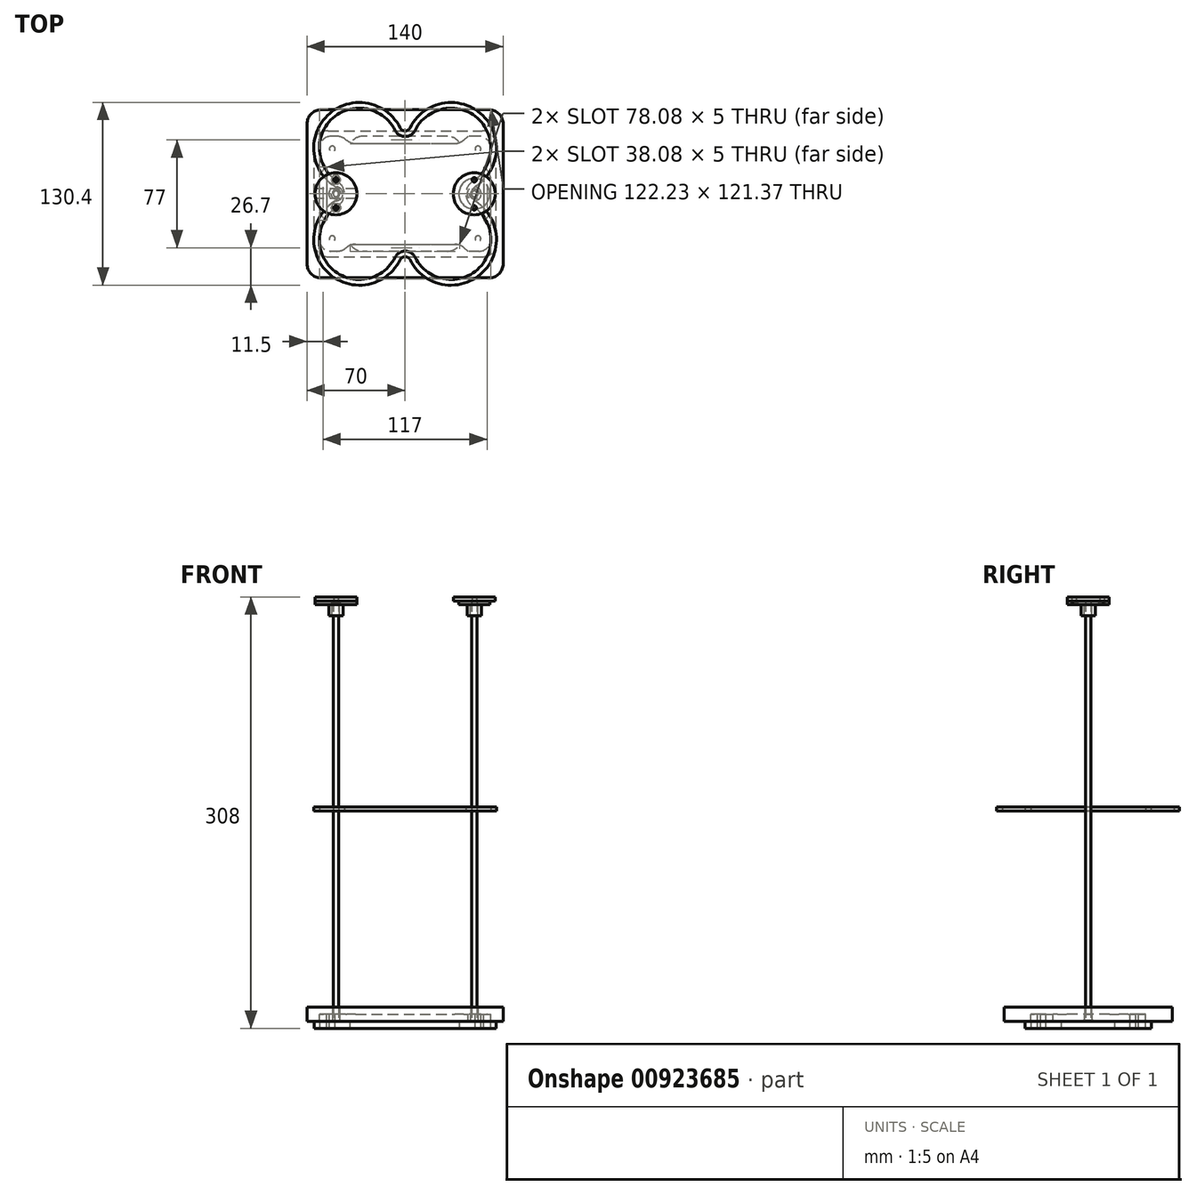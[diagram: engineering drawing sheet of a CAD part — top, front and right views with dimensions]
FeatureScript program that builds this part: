
annotation { "Feature Type Name" : "Feature", "Feature Type Description" : "" }
export const myFeature = defineFeature(function(context is Context, id is Id, definition is map)
    precondition{}
    {
        {
            var Q0;
            Q0=qCreatedBy(makeId("Top.planeOp"),FACE);
            var sketch = newSketch(context, id + "F0", { "sketchPlane" : qUnion([Q0])});
            skArc(sketch, "E0", {"start": v(50.3, 5.38) * mm, "mid": v(54.36, 56.94) * mm, "end": v(3.58, 47.14) * mm});
            skArc(sketch, "E1.MirrorC", {"start": v(-50.3, 5.38) * mm, "mid": v(-54.36, 56.94) * mm, "end": v(-3.58, 47.14) * mm});
            skArc(sketch, "E2.MirrorC", {"start": v(50.3, -5.38) * mm, "mid": v(54.36, -56.94) * mm, "end": v(3.58, -47.14) * mm});
            skArc(sketch, "E3.MirrorC", {"start": v(-50.3, -5.38) * mm, "mid": v(-54.36, -56.94) * mm, "end": v(-3.58, -47.14) * mm});
            skLineSegment(sketch, "E4", {"start": v(-32.7, -32.7) * mm, "end": v(32.7, 32.7) * mm, "construction": true});
            skArc(sketch, "E5", {"start": v(50.3, 5.38) * mm, "mid": v(47.37, 0) * mm, "end": v(50.3, -5.38) * mm});
            skArc(sketch, "E6.MirrorC", {"start": v(-50.3, 5.38) * mm, "mid": v(-47.37, 0) * mm, "end": v(-50.3, -5.38) * mm});
            skArc(sketch, "E7", {"start": v(-3.58, 47.14) * mm, "mid": v(0, 44.91) * mm, "end": v(3.58, 47.14) * mm});
            skArc(sketch, "E8.MirrorC", {"start": v(-3.58, -47.14) * mm, "mid": v(0, -44.91) * mm, "end": v(3.58, -47.14) * mm});
            skArc(sketch, "E9.0", {"start": v(-48.14, 8.74) * mm, "mid": v(-43.37, 0) * mm, "end": v(-48.14, -8.74) * mm});
            skArc(sketch, "E9.1", {"start": v(-48.14, -8.74) * mm, "mid": v(-51.7, -53.95) * mm, "end": v(-7.17, -45.36) * mm});
            skArc(sketch, "E9.2", {"start": v(-48.14, 8.74) * mm, "mid": v(-51.7, 53.95) * mm, "end": v(-7.17, 45.36) * mm});
            skArc(sketch, "E9.3", {"start": v(-7.17, -45.36) * mm, "mid": v(0, -40.91) * mm, "end": v(7.17, -45.36) * mm});
            skArc(sketch, "E9.4", {"start": v(-7.17, 45.36) * mm, "mid": v(0, 40.91) * mm, "end": v(7.17, 45.36) * mm});
            skArc(sketch, "E9.5", {"start": v(48.14, 8.74) * mm, "mid": v(51.7, 53.95) * mm, "end": v(7.17, 45.36) * mm});
            skArc(sketch, "E9.6", {"start": v(48.14, 8.74) * mm, "mid": v(43.37, 0) * mm, "end": v(48.14, -8.74) * mm});
            skArc(sketch, "E9.7", {"start": v(48.14, -8.74) * mm, "mid": v(51.7, -53.95) * mm, "end": v(7.17, -45.36) * mm});
            skSolve(sketch);
        }
        {
            var Q0;
            Q0 = qSketchRegion(id + "F0", true);
            extrude(context, id + "F1", {"entities" : qUnion([Q0]), "depth" : 3 * mm, "offsetDistance" : 25 * mm});
        }
        {
            var Q0;
            Q0=qCreatedBy(makeId("Top.planeOp"),FACE);
            var sketch = newSketch(context, id + "F2", { "sketchPlane" : qUnion([Q0])});
            skCircle(sketch, "E10", {"center": v(49.37, 0) * mm, "radius": 2 * mm});
            skCircle(sketch, "E11.MirrorC", {"center": v(-49.37, 0) * mm, "radius": 2 * mm});
            skSolve(sketch);
        }
        {
            var Q0;
            Q0 = qSketchRegion(id + "F2", true);
            extrude(context, id + "F3", {"entities" : qUnion([Q0]), "operationType" : NewBodyOperationType.ADD, "depth" : 150 * mm, "offsetDistance" : 25 * mm, "hasSecondDirection" : true, "secondDirectionOppositeDirection" : true, "secondDirectionDepth" : 150 * mm});
        }
        {
            var Q0;
            Q0=qCreatedBy(makeId("Top.planeOp"),FACE);
            cPlane(context, id + "F4", {"entities" : qUnion([Q0]), "cplaneType" : CPlaneType.OFFSET, "offset" : 150 * mm, "oppositeDirection" : true, "width" : 150 * mm, "height" : 150 * mm});
        }
        {
            var Q0;
            Q0=qCreatedBy(id+"F4.planeOp",FACE);
            var sketch = newSketch(context, id + "F5", { "sketchPlane" : qUnion([Q0])});
            skLineSegment(sketch, "E12.bottom", {"start": v(-65, -45) * mm, "end": v(65, -45) * mm});
            skLineSegment(sketch, "E12.top", {"start": v(-65, 45) * mm, "end": v(65, 45) * mm});
            skLineSegment(sketch, "E12.left", {"start": v(-65, -45) * mm, "end": v(-65, 45) * mm});
            skLineSegment(sketch, "E12.right", {"start": v(65, -45) * mm, "end": v(65, 45) * mm});
            skSolve(sketch);
        }
        {
            var Q0;
            Q0 = qSketchRegion(id + "F5", true);
            extrude(context, id + "F6", {"entities" : qUnion([Q0]), "oppositeDirection" : true, "depth" : 5 * mm, "offsetDistance" : 25 * mm});
        }
        {
            var Q0;
            Q0=makeQuery(id+"F6.opExtrude","SWEPT_EDGE",EDGE,{"disambiguationData":[OSD([sQuery(id+"F5.wireOp",EDGE,"E12.bottom"),sQuery(id+"F5.wireOp",EDGE,"E12.left")])]});
            var Q1;
            Q1=makeQuery(id+"F6.opExtrude","SWEPT_EDGE",EDGE,{"disambiguationData":[OSD([sQuery(id+"F5.wireOp",EDGE,"E12.top"),sQuery(id+"F5.wireOp",EDGE,"E12.left")])]});
            var Q2;
            Q2=makeQuery(id+"F6.opExtrude","SWEPT_EDGE",EDGE,{"disambiguationData":[OSD([sQuery(id+"F5.wireOp",EDGE,"E12.bottom"),sQuery(id+"F5.wireOp",EDGE,"E12.right")])]});
            var Q3;
            Q3=makeQuery(id+"F6.opExtrude","SWEPT_EDGE",EDGE,{"disambiguationData":[OSD([sQuery(id+"F5.wireOp",EDGE,"E12.top"),sQuery(id+"F5.wireOp",EDGE,"E12.right")])]});
            fillet(context, id + "F7", {"entities" : qUnion([Q0, Q1, Q2, Q3]), "radius" : 10 * mm, "tangentPropagation" : true, "allowEdgeOverflow" : false});
        }
        {
            var Q0;
            Q0=makeQuery(id+"F3.opExtrude","CAP_FACE",FACE,{"disambiguationData":[OSD([sQuery(id+"F2.wireOp",EDGE,"E10")])],"isStart":true});
            var sketch = newSketch(context, id + "F8", { "sketchPlane" : qUnion([Q0])});
            skCircle(sketch, "E13", {"center": v(49.37, 0) * mm, "radius": 3.5 * mm});
            skCircle(sketch, "E14.MirrorC", {"center": v(-49.37, 0) * mm, "radius": 3.5 * mm});
            skSolve(sketch);
        }
        {
            var Q0;
            Q0 = qSketchRegion(id + "F8", true);
            extrude(context, id + "F9", {"entities" : qUnion([Q0]), "operationType" : NewBodyOperationType.ADD, "oppositeDirection" : true, "depth" : 0.5 * mm, "offsetDistance" : 25 * mm});
        }
        {
            var Q0;
            Q0=qCreatedBy(id+"F4.planeOp",FACE);
            var sketch = newSketch(context, id + "F10", { "sketchPlane" : qUnion([Q0])});
            skLineSegment(sketch, "E15.bottom", {"start": v(61, -41) * mm, "end": v(-61, -41) * mm});
            skLineSegment(sketch, "E15.top", {"start": v(61, 41) * mm, "end": v(-61, 41) * mm});
            skLineSegment(sketch, "E15.left", {"start": v(61, -41) * mm, "end": v(61, 41) * mm});
            skLineSegment(sketch, "E15.right", {"start": v(-61, -41) * mm, "end": v(-61, 41) * mm});
            skCircle(sketch, "E16", {"center": v(49.37, 0) * mm, "radius": 2.65 * mm});
            skCircle(sketch, "E17.MirrorC", {"center": v(-49.37, 0) * mm, "radius": 2.65 * mm});
            skSolve(sketch);
        }
        {
            var Q0;
            Q0 = qSketchRegion(id + "F10", true);
            extrude(context, id + "F11", {"entities" : qUnion([Q0]), "depth" : 5 * mm, "offsetDistance" : 25 * mm});
        }
        {
            var Q0;
            Q0=makeQuery(id+"F11.opExtrude","SWEPT_EDGE",EDGE,{"disambiguationData":[OSD([sQuery(id+"F10.wireOp",EDGE,"E15.top"),sQuery(id+"F10.wireOp",EDGE,"E15.left")])]});
            var Q1;
            Q1=makeQuery(id+"F11.opExtrude","SWEPT_EDGE",EDGE,{"disambiguationData":[OSD([sQuery(id+"F10.wireOp",EDGE,"E15.top"),sQuery(id+"F10.wireOp",EDGE,"E15.right")])]});
            var Q2;
            Q2=makeQuery(id+"F11.opExtrude","SWEPT_EDGE",EDGE,{"disambiguationData":[OSD([sQuery(id+"F10.wireOp",EDGE,"E15.bottom"),sQuery(id+"F10.wireOp",EDGE,"E15.right")])]});
            var Q3;
            Q3=makeQuery(id+"F11.opExtrude","SWEPT_EDGE",EDGE,{"disambiguationData":[OSD([sQuery(id+"F10.wireOp",EDGE,"E15.bottom"),sQuery(id+"F10.wireOp",EDGE,"E15.left")])]});
            fillet(context, id + "F12", {"entities" : qUnion([Q0, Q1, Q2, Q3]), "radius" : 8 * mm, "tangentPropagation" : true, "allowEdgeOverflow" : false});
        }
        {
            var Q0;
            Q0=makeQuery(id+"F11.opExtrude","CAP_FACE",FACE,{"disambiguationData":[OSD([sQuery(id+"F10.wireOp",EDGE,"E15.bottom"),sQuery(id+"F10.wireOp",EDGE,"E15.top"),sQuery(id+"F10.wireOp",EDGE,"E15.left"),sQuery(id+"F10.wireOp",EDGE,"E15.right"),sQuery(id+"F10.wireOp",EDGE,"E16"),sQuery(id+"F10.wireOp",EDGE,"E17.MirrorC")])],"isStart":false});
            var sketch = newSketch(context, id + "F13", { "sketchPlane" : qUnion([Q0])});
            skLineSegment(sketch, "E18", {"start": v(-61, 25) * mm, "end": v(-56, 19.04) * mm});
            skLineSegment(sketch, "E19", {"start": v(-56, 19.04) * mm, "end": v(-56, -19.04) * mm});
            skLineSegment(sketch, "E20", {"start": v(-56, -19.04) * mm, "end": v(-61, -25) * mm});
            skLineSegment(sketch, "E21", {"start": v(-45, 41) * mm, "end": v(-39.04, 36) * mm});
            skLineSegment(sketch, "E22", {"start": v(-39.04, 36) * mm, "end": v(39.04, 36) * mm});
            skLineSegment(sketch, "E23", {"start": v(39.04, 36) * mm, "end": v(45, 41) * mm});
            skLineSegment(sketch, "E24", {"start": v(45, 41) * mm, "end": v(-45, 41) * mm});
            skLineSegment(sketch, "E25", {"start": v(-61, 25) * mm, "end": v(-61, -25) * mm});
            skLineSegment(sketch, "E26.MirrorCS", {"start": v(-45, -41) * mm, "end": v(-39.04, -36) * mm});
            skLineSegment(sketch, "E27.MirrorCS", {"start": v(-39.04, -36) * mm, "end": v(39.04, -36) * mm});
            skLineSegment(sketch, "E28.MirrorCS", {"start": v(39.04, -36) * mm, "end": v(45, -41) * mm});
            skLineSegment(sketch, "E29.MirrorCS", {"start": v(45, -41) * mm, "end": v(-45, -41) * mm});
            skLineSegment(sketch, "E30.MirrorCS", {"start": v(56, 19.04) * mm, "end": v(56, -19.04) * mm});
            skLineSegment(sketch, "E31.MirrorCS", {"start": v(61, 25) * mm, "end": v(56, 19.04) * mm});
            skLineSegment(sketch, "E32.MirrorCS", {"start": v(61, 25) * mm, "end": v(61, -25) * mm});
            skLineSegment(sketch, "E33.MirrorCS", {"start": v(56, -19.04) * mm, "end": v(61, -25) * mm});
            skSolve(sketch);
        }
        {
            var Q0;
            Q0 = qSketchRegion(id + "F13", true);
            extrude(context, id + "F14", {"entities" : qUnion([Q0]), "operationType" : NewBodyOperationType.REMOVE, "oppositeDirection" : true, "depth" : 25 * mm, "offsetDistance" : 25 * mm});
        }
        {
            var Q0;
            Q0=makeQuery(id+"F14.boolean.opBoolean","COPY",EDGE,{"derivedFrom":makeQuery(id+"F14.opExtrude","SWEPT_EDGE",EDGE,{"disambiguationData":[OSD([sQuery(id+"F10.wireOp",EDGE,"E15.right"),sQuery(id+"F13.wireOp",EDGE,"E18"),sQuery(id+"F13.wireOp",EDGE,"E25")])]})});
            var Q1;
            Q1=makeQuery(id+"F14.boolean.opBoolean","COPY",EDGE,{"derivedFrom":makeQuery(id+"F14.opExtrude","SWEPT_EDGE",EDGE,{"disambiguationData":[OSD([sQuery(id+"F10.wireOp",EDGE,"E15.right"),sQuery(id+"F13.wireOp",EDGE,"E20"),sQuery(id+"F13.wireOp",EDGE,"E25")])]})});
            var Q2;
            Q2=makeQuery(id+"F14.boolean.opBoolean","COPY",EDGE,{"derivedFrom":makeQuery(id+"F14.opExtrude","SWEPT_EDGE",EDGE,{"disambiguationData":[OSD([sQuery(id+"F10.wireOp",EDGE,"E15.bottom"),sQuery(id+"F13.wireOp",EDGE,"E26.MirrorCS"),sQuery(id+"F13.wireOp",EDGE,"E29.MirrorCS")])]})});
            var Q3;
            Q3=makeQuery(id+"F14.boolean.opBoolean","COPY",EDGE,{"derivedFrom":makeQuery(id+"F14.opExtrude","SWEPT_EDGE",EDGE,{"disambiguationData":[OSD([sQuery(id+"F10.wireOp",EDGE,"E15.bottom"),sQuery(id+"F13.wireOp",EDGE,"E28.MirrorCS"),sQuery(id+"F13.wireOp",EDGE,"E29.MirrorCS")])]})});
            var Q4;
            Q4=makeQuery(id+"F14.boolean.opBoolean","COPY",EDGE,{"derivedFrom":makeQuery(id+"F14.opExtrude","SWEPT_EDGE",EDGE,{"disambiguationData":[OSD([sQuery(id+"F10.wireOp",EDGE,"E15.left"),sQuery(id+"F13.wireOp",EDGE,"E32.MirrorCS"),sQuery(id+"F13.wireOp",EDGE,"E33.MirrorCS")])]})});
            var Q5;
            Q5=makeQuery(id+"F14.boolean.opBoolean","COPY",EDGE,{"derivedFrom":makeQuery(id+"F14.opExtrude","SWEPT_EDGE",EDGE,{"disambiguationData":[OSD([sQuery(id+"F10.wireOp",EDGE,"E15.left"),sQuery(id+"F13.wireOp",EDGE,"E31.MirrorCS"),sQuery(id+"F13.wireOp",EDGE,"E32.MirrorCS")])]})});
            var Q6;
            Q6=makeQuery(id+"F14.boolean.opBoolean","COPY",EDGE,{"derivedFrom":makeQuery(id+"F14.opExtrude","SWEPT_EDGE",EDGE,{"disambiguationData":[OSD([sQuery(id+"F10.wireOp",EDGE,"E15.top"),sQuery(id+"F13.wireOp",EDGE,"E23"),sQuery(id+"F13.wireOp",EDGE,"E24")])]})});
            var Q7;
            Q7=makeQuery(id+"F14.boolean.opBoolean","COPY",EDGE,{"derivedFrom":makeQuery(id+"F14.opExtrude","SWEPT_EDGE",EDGE,{"disambiguationData":[OSD([sQuery(id+"F10.wireOp",EDGE,"E15.top"),sQuery(id+"F13.wireOp",EDGE,"E21"),sQuery(id+"F13.wireOp",EDGE,"E24")])]})});
            fillet(context, id + "F15", {"entities" : qUnion([Q0, Q1, Q2, Q3, Q4, Q5, Q6, Q7]), "radius" : 10 * mm, "tangentPropagation" : true, "allowEdgeOverflow" : false});
        }
        {
            var Q0;
            Q0=makeQuery(id+"F14.boolean.opBoolean","COPY",EDGE,{"derivedFrom":makeQuery(id+"F14.opExtrude","SWEPT_EDGE",EDGE,{"disambiguationData":[OSD([sQuery(id+"F13.wireOp",EDGE,"E21"),sQuery(id+"F13.wireOp",EDGE,"E22")])]})});
            var Q1;
            Q1=makeQuery(id+"F14.boolean.opBoolean","COPY",EDGE,{"derivedFrom":makeQuery(id+"F14.opExtrude","SWEPT_EDGE",EDGE,{"disambiguationData":[OSD([sQuery(id+"F13.wireOp",EDGE,"E22"),sQuery(id+"F13.wireOp",EDGE,"E23")])]})});
            var Q2;
            Q2=makeQuery(id+"F14.boolean.opBoolean","COPY",EDGE,{"derivedFrom":makeQuery(id+"F14.opExtrude","SWEPT_EDGE",EDGE,{"disambiguationData":[OSD([sQuery(id+"F13.wireOp",EDGE,"E30.MirrorCS"),sQuery(id+"F13.wireOp",EDGE,"E31.MirrorCS")])]})});
            var Q3;
            Q3=makeQuery(id+"F14.boolean.opBoolean","COPY",EDGE,{"derivedFrom":makeQuery(id+"F14.opExtrude","SWEPT_EDGE",EDGE,{"disambiguationData":[OSD([sQuery(id+"F13.wireOp",EDGE,"E30.MirrorCS"),sQuery(id+"F13.wireOp",EDGE,"E33.MirrorCS")])]})});
            var Q4;
            Q4=makeQuery(id+"F14.boolean.opBoolean","COPY",EDGE,{"derivedFrom":makeQuery(id+"F14.opExtrude","SWEPT_EDGE",EDGE,{"disambiguationData":[OSD([sQuery(id+"F13.wireOp",EDGE,"E27.MirrorCS"),sQuery(id+"F13.wireOp",EDGE,"E28.MirrorCS")])]})});
            var Q5;
            Q5=makeQuery(id+"F14.boolean.opBoolean","COPY",EDGE,{"derivedFrom":makeQuery(id+"F14.opExtrude","SWEPT_EDGE",EDGE,{"disambiguationData":[OSD([sQuery(id+"F13.wireOp",EDGE,"E26.MirrorCS"),sQuery(id+"F13.wireOp",EDGE,"E27.MirrorCS")])]})});
            var Q6;
            Q6=makeQuery(id+"F14.boolean.opBoolean","COPY",EDGE,{"derivedFrom":makeQuery(id+"F14.opExtrude","SWEPT_EDGE",EDGE,{"disambiguationData":[OSD([sQuery(id+"F13.wireOp",EDGE,"E19"),sQuery(id+"F13.wireOp",EDGE,"E20")])]})});
            var Q7;
            Q7=makeQuery(id+"F14.boolean.opBoolean","COPY",EDGE,{"derivedFrom":makeQuery(id+"F14.opExtrude","SWEPT_EDGE",EDGE,{"disambiguationData":[OSD([sQuery(id+"F13.wireOp",EDGE,"E18"),sQuery(id+"F13.wireOp",EDGE,"E19")])]})});
            fillet(context, id + "F16", {"entities" : qUnion([Q0, Q1, Q2, Q3, Q4, Q5, Q6, Q7]), "radius" : 10 * mm, "tangentPropagation" : true, "allowEdgeOverflow" : false});
        }
        {
            var Q0;
            Q0=qCreatedBy(id+"F4.planeOp",FACE);
            var sketch = newSketch(context, id + "F17", { "sketchPlane" : qUnion([Q0])});
            skCircle(sketch, "E34", {"center": v(52, 32) * mm, "radius": 2.05 * mm});
            skCircle(sketch, "E35.MirrorC", {"center": v(52, -32) * mm, "radius": 2.05 * mm});
            skCircle(sketch, "E36.MirrorC", {"center": v(-52, -32) * mm, "radius": 2.05 * mm});
            skCircle(sketch, "E37.MirrorC", {"center": v(-52, 32) * mm, "radius": 2.05 * mm});
            skSolve(sketch);
        }
        {
            var Q0;
            Q0 = qSketchRegion(id + "F17", true);
            extrude(context, id + "F18", {"entities" : qUnion([Q0]), "operationType" : NewBodyOperationType.REMOVE, "endBound" : BoundingType.SYMMETRIC, "oppositeDirection" : true, "depth" : 25 * mm, "offsetDistance" : 25 * mm});
        }
        {
            var Q0;
            Q0=qCreatedBy(makeId("Top.planeOp"),FACE);
            cPlane(context, id + "F19", {"entities" : qUnion([Q0]), "cplaneType" : CPlaneType.OFFSET, "offset" : 150 * mm, "width" : 150 * mm, "height" : 150 * mm});
        }
        {
            var Q0;
            Q0=qCreatedBy(id+"F19.planeOp",FACE);
            var sketch = newSketch(context, id + "F20", { "sketchPlane" : qUnion([Q0])});
            skCircle(sketch, "E38", {"center": v(-49.37, 0) * mm, "radius": 15 * mm});
            skCircle(sketch, "E39.MirrorC", {"center": v(49.37, 0) * mm, "radius": 15 * mm});
            skCircle(sketch, "E40", {"center": v(-49.37, 10) * mm, "radius": 1.55 * mm});
            skCircle(sketch, "E41.MirrorC", {"center": v(-49.37, -10) * mm, "radius": 1.55 * mm});
            skCircle(sketch, "E42.MirrorC", {"center": v(49.37, -10) * mm, "radius": 1.55 * mm});
            skCircle(sketch, "E43.MirrorC", {"center": v(49.37, 10) * mm, "radius": 1.55 * mm});
            skSolve(sketch);
        }
        {
            var Q0;
            Q0 = qSketchRegion(id + "F20", true);
            extrude(context, id + "F21", {"entities" : qUnion([Q0]), "depth" : 3 * mm, "offsetDistance" : 25 * mm});
        }
        {
            var Q0;
            Q0=qCreatedBy(id+"F19.planeOp",FACE);
            var sketch = newSketch(context, id + "F22", { "sketchPlane" : qUnion([Q0])});
            skCircle(sketch, "E44", {"center": v(-49.37, 0) * mm, "radius": 15 * mm});
            skCircle(sketch, "E45", {"center": v(-49.37, 0) * mm, "radius": 2.7 * mm});
            skCircle(sketch, "E46", {"center": v(-49.37, 10) * mm, "radius": 1.8 * mm});
            skCircle(sketch, "E47.MirrorC", {"center": v(-49.37, -10) * mm, "radius": 1.8 * mm});
            skCircle(sketch, "E48.MirrorC", {"center": v(49.37, -10) * mm, "radius": 1.8 * mm});
            skCircle(sketch, "E49.MirrorC", {"center": v(49.37, 10) * mm, "radius": 1.8 * mm});
            skCircle(sketch, "E50.MirrorC", {"center": v(49.37, 0) * mm, "radius": 15 * mm});
            skCircle(sketch, "E51.MirrorC", {"center": v(49.37, 0) * mm, "radius": 2.7 * mm});
            skSolve(sketch);
        }
        {
            var Q0;
            Q0 = qSketchRegion(id + "F22", true);
            extrude(context, id + "F23", {"entities" : qUnion([Q0]), "oppositeDirection" : true, "depth" : 2.5 * mm, "offsetDistance" : 25 * mm});
        }
        {
            var Q0;
            Q0=makeQuery(id+"F23.opExtrude","CAP_FACE",FACE,{"disambiguationData":[OSD([sQuery(id+"F22.wireOp",EDGE,"E45"),sQuery(id+"F22.wireOp",EDGE,"E46"),sQuery(id+"F22.wireOp",EDGE,"E44"),sQuery(id+"F22.wireOp",EDGE,"E47.MirrorC")])],"isStart":false});
            var sketch = newSketch(context, id + "F24", { "sketchPlane" : qUnion([Q0])});
            skCircle(sketch, "E52", {"center": v(-49.37, 0) * mm, "radius": 2.7 * mm});
            skCircle(sketch, "E53", {"center": v(-49.37, 0) * mm, "radius": 5 * mm});
            skCircle(sketch, "E54.MirrorC", {"center": v(49.37, 0) * mm, "radius": 5 * mm});
            skCircle(sketch, "E55.MirrorC", {"center": v(49.37, 0) * mm, "radius": 2.7 * mm});
            skSolve(sketch);
        }
        {
            var Q0;
            Q0 = qSketchRegion(id + "F24", true);
            extrude(context, id + "F25", {"entities" : qUnion([Q0]), "operationType" : NewBodyOperationType.ADD, "depth" : 8 * mm, "offsetDistance" : 25 * mm});
        }
        {
            var Q0;
            Q0=makeQuery(id+"F23.opExtrude","CAP_FACE",FACE,{"disambiguationData":[OSD([sQuery(id+"F22.wireOp",EDGE,"E48.MirrorC"),sQuery(id+"F22.wireOp",EDGE,"E49.MirrorC"),sQuery(id+"F22.wireOp",EDGE,"E50.MirrorC"),sQuery(id+"F22.wireOp",EDGE,"E51.MirrorC")])],"isStart":true});
            var sketch = newSketch(context, id + "F26", { "sketchPlane" : qUnion([Q0])});
            skLineSegment(sketch, "E56.bottom", {"start": v(75, 3.5) * mm, "end": v(-75, 3.5) * mm});
            skLineSegment(sketch, "E56.top", {"start": v(75, -3.5) * mm, "end": v(-75, -3.5) * mm});
            skLineSegment(sketch, "E56.left", {"start": v(75, 3.5) * mm, "end": v(75, -3.5) * mm});
            skLineSegment(sketch, "E56.right", {"start": v(-75, 3.5) * mm, "end": v(-75, -3.5) * mm});
            skSolve(sketch);
        }
        {
            var Q0;
            Q0 = qSketchRegion(id + "F26", true);
            extrude(context, id + "F27", {"entities" : qUnion([Q0]), "operationType" : NewBodyOperationType.REMOVE, "oppositeDirection" : true, "depth" : 0.3 * mm, "offsetDistance" : 25 * mm});
        }
        {
            var Q0;
            Q0=makeQuery(id+"F23.opExtrude","CAP_FACE",FACE,{"disambiguationData":[OSD([sQuery(id+"F22.wireOp",EDGE,"E45"),sQuery(id+"F22.wireOp",EDGE,"E46"),sQuery(id+"F22.wireOp",EDGE,"E44"),sQuery(id+"F22.wireOp",EDGE,"E47.MirrorC")])],"isStart":false});
            var sketch = newSketch(context, id + "F28", { "sketchPlane" : qUnion([Q0])});
            skCircle(sketch, "E57", {"center": v(-49.37, -10) * mm, "radius": 3.46 * mm, "construction": true});
            skLineSegment(sketch, "E58", {"start": v(-51.1, -7) * mm, "end": v(-47.64, -7) * mm});
            skLineSegment(sketch, "E59", {"start": v(-47.64, -7) * mm, "end": v(-45.9, -10) * mm});
            skLineSegment(sketch, "E60", {"start": v(-45.9, -10) * mm, "end": v(-47.64, -13) * mm});
            skLineSegment(sketch, "E61", {"start": v(-47.64, -13) * mm, "end": v(-51.1, -13) * mm});
            skLineSegment(sketch, "E62", {"start": v(-51.1, -13) * mm, "end": v(-52.83, -10) * mm});
            skLineSegment(sketch, "E63", {"start": v(-52.83, -10) * mm, "end": v(-51.1, -7) * mm});
            skLineSegment(sketch, "E64.MirrorCS", {"start": v(-47.64, 7) * mm, "end": v(-45.9, 10) * mm});
            skLineSegment(sketch, "E65.MirrorCS", {"start": v(-51.1, 7) * mm, "end": v(-47.64, 7) * mm});
            skLineSegment(sketch, "E66.MirrorCS", {"start": v(-45.9, 10) * mm, "end": v(-47.64, 13) * mm});
            skLineSegment(sketch, "E67.MirrorCS", {"start": v(-51.1, 13) * mm, "end": v(-52.83, 10) * mm});
            skLineSegment(sketch, "E68.MirrorCS", {"start": v(-52.83, 10) * mm, "end": v(-51.1, 7) * mm});
            skLineSegment(sketch, "E69.MirrorCS", {"start": v(-47.64, 13) * mm, "end": v(-51.1, 13) * mm});
            skLineSegment(sketch, "E70.MirrorCS", {"start": v(45.9, -10) * mm, "end": v(47.64, -13) * mm});
            skLineSegment(sketch, "E71.MirrorCS", {"start": v(47.64, -13) * mm, "end": v(51.1, -13) * mm});
            skLineSegment(sketch, "E72.MirrorCS", {"start": v(51.1, 13) * mm, "end": v(52.83, 10) * mm});
            skLineSegment(sketch, "E73.MirrorCS", {"start": v(45.9, 10) * mm, "end": v(47.64, 13) * mm});
            skLineSegment(sketch, "E74.MirrorCS", {"start": v(51.1, 7) * mm, "end": v(47.64, 7) * mm});
            skLineSegment(sketch, "E75.MirrorCS", {"start": v(51.1, -7) * mm, "end": v(47.64, -7) * mm});
            skLineSegment(sketch, "E76.MirrorCS", {"start": v(47.64, -7) * mm, "end": v(45.9, -10) * mm});
            skLineSegment(sketch, "E77.MirrorCS", {"start": v(52.83, -10) * mm, "end": v(51.1, -7) * mm});
            skLineSegment(sketch, "E78.MirrorCS", {"start": v(52.83, 10) * mm, "end": v(51.1, 7) * mm});
            skLineSegment(sketch, "E79.MirrorCS", {"start": v(47.64, 7) * mm, "end": v(45.9, 10) * mm});
            skLineSegment(sketch, "E80.MirrorCS", {"start": v(51.1, -13) * mm, "end": v(52.83, -10) * mm});
            skLineSegment(sketch, "E81.MirrorCS", {"start": v(47.64, 13) * mm, "end": v(51.1, 13) * mm});
            skSolve(sketch);
        }
        {
            var Q0;
            Q0 = qSketchRegion(id + "F28", true);
            extrude(context, id + "F29", {"entities" : qUnion([Q0]), "operationType" : NewBodyOperationType.REMOVE, "oppositeDirection" : true, "depth" : 1 * mm, "offsetDistance" : 25 * mm});
        }
        {
            var Q0;
            Q0=qCreatedBy(id+"F4.planeOp",FACE);
            var sketch = newSketch(context, id + "F30", { "sketchPlane" : qUnion([Q0])});
            skLineSegment(sketch, "E82.bottom", {"start": v(70, -60) * mm, "end": v(-70, -60) * mm});
            skLineSegment(sketch, "E82.top", {"start": v(70, 60) * mm, "end": v(-70, 60) * mm});
            skLineSegment(sketch, "E82.left", {"start": v(70, -60) * mm, "end": v(70, 60) * mm});
            skLineSegment(sketch, "E82.right", {"start": v(-70, -60) * mm, "end": v(-70, 60) * mm});
            skCircle(sketch, "E83", {"center": v(49.37, 0) * mm, "radius": 2.42 * mm});
            skCircle(sketch, "E84.MirrorC", {"center": v(-49.37, 0) * mm, "radius": 2.42 * mm});
            skSolve(sketch);
        }
        {
            var Q0;
            Q0=makeQuery(id+"F30.imprint","IMPRINT",FACE,{"disambiguationData":[TD([[makeQuery(id+"F30.imprint","IMPRINT",EDGE,{"derivedFrom":sQuery(id+"F30.wireOp",EDGE,"E82.bottom")}),-1.0]])]});
            extrude(context, id + "F31", {"entities" : qUnion([Q0]), "depth" : 10 * mm, "offsetDistance" : 25 * mm});
        }
        {
            var Q0;
            Q0=makeQuery(id+"F31.opExtrude","SWEPT_EDGE",EDGE,{"disambiguationData":[OSD([sQuery(id+"F30.wireOp",EDGE,"E82.bottom"),sQuery(id+"F30.wireOp",EDGE,"E82.left")])]});
            var Q1;
            Q1=makeQuery(id+"F31.opExtrude","SWEPT_EDGE",EDGE,{"disambiguationData":[OSD([sQuery(id+"F30.wireOp",EDGE,"E82.bottom"),sQuery(id+"F30.wireOp",EDGE,"E82.right")])]});
            var Q2;
            Q2=makeQuery(id+"F31.opExtrude","SWEPT_EDGE",EDGE,{"disambiguationData":[OSD([sQuery(id+"F30.wireOp",EDGE,"E82.top"),sQuery(id+"F30.wireOp",EDGE,"E82.left")])]});
            var Q3;
            Q3=makeQuery(id+"F31.opExtrude","SWEPT_EDGE",EDGE,{"disambiguationData":[OSD([sQuery(id+"F30.wireOp",EDGE,"E82.top"),sQuery(id+"F30.wireOp",EDGE,"E82.right")])]});
            fillet(context, id + "F32", {"entities" : qUnion([Q0, Q1, Q2, Q3]), "radius" : 10 * mm, "tangentPropagation" : true, "allowEdgeOverflow" : false});
        }
        {
            var Q0;
            Q0=makeQuery(id+"F23.opExtrude","SWEPT_BODY",BODY,{"disambiguationData":[OSD([sQuery(id+"F22.wireOp",EDGE,"E48.MirrorC"),sQuery(id+"F22.wireOp",EDGE,"E49.MirrorC"),sQuery(id+"F22.wireOp",EDGE,"E50.MirrorC"),sQuery(id+"F22.wireOp",EDGE,"E51.MirrorC")])]});
            transform(context, id + "F33", {"entities" : qUnion([Q0]), "transformType" : TransformType.TRANSLATION_3D, "dx" : 0 * mm, "dy" : 0 * mm, "dz" : 0 * mm, "makeCopy" : true});
        }
        {
            var Q0;
            {var subQ0=sQuery(id+"F22.wireOp",EDGE,"E48.MirrorC");var subQ1=sQuery(id+"F22.wireOp",EDGE,"E50.MirrorC");Q0=makeQuery(id+"F33.opPattern","COPY",FACE,{"derivedFrom":makeQuery(id+"F27.boolean.opBoolean","SPLIT",FACE,{"disambiguationData":[TD([makeQuery(id+"F23.opExtrude","SWEPT_FACE",FACE,{"disambiguationData":[OSD([subQ0])]})])],"derivedFrom":makeQuery(id+"F23.opExtrude","CAP_FACE",FACE,{"disambiguationData":[OSD([subQ0,sQuery(id+"F22.wireOp",EDGE,"E49.MirrorC"),subQ1,sQuery(id+"F22.wireOp",EDGE,"E51.MirrorC")])],"isStart":true})}),"instanceName":"1"});}
            var sketch = newSketch(context, id + "F34", { "sketchPlane" : qUnion([Q0])});
            skCircle(sketch, "E85", {"center": v(49.37, 0) * mm, "radius": 15 * mm});
            skCircle(sketch, "E86", {"center": v(49.37, 0) * mm, "radius": 2.7 * mm});
            skSolve(sketch);
        }
        {
            var Q0;
            Q0 = qSketchRegion(id + "F34", true);
            var Q1;
            Q1=makeQuery(id+"F33.opPattern","COPY",FACE,{"derivedFrom":makeQuery(id+"F23.opExtrude","CAP_FACE",FACE,{"disambiguationData":[OSD([sQuery(id+"F22.wireOp",EDGE,"E48.MirrorC"),sQuery(id+"F22.wireOp",EDGE,"E49.MirrorC"),sQuery(id+"F22.wireOp",EDGE,"E50.MirrorC"),sQuery(id+"F22.wireOp",EDGE,"E51.MirrorC")])],"isStart":false}),"instanceName":"1"});
            extrude(context, id + "F35", {"entities" : qUnion([Q0]), "operationType" : NewBodyOperationType.ADD, "endBound" : BoundingType.UP_TO_SURFACE, "oppositeDirection" : true, "depth" : 25 * mm, "endBoundEntityFace" : qUnion([Q1]), "offsetDistance" : 25 * mm});
        }
        {
            var Q0;
            {var subQ0=sQuery(id+"F22.wireOp",EDGE,"E49.MirrorC");var subQ1=sQuery(id+"F22.wireOp",EDGE,"E50.MirrorC");var subQ3=sQuery(id+"F22.wireOp",EDGE,"E48.MirrorC");var subQ4=makeQuery(id+"F23.opExtrude","CAP_FACE",FACE,{"disambiguationData":[OSD([subQ3,subQ0,subQ1,sQuery(id+"F22.wireOp",EDGE,"E51.MirrorC")])],"isStart":true});Q0=makeQuery(id+"F35.boolean.opBoolean","MERGE",FACE,{"derivedFrom":[makeQuery(id+"F33.opPattern","COPY",FACE,{"derivedFrom":makeQuery(id+"F27.boolean.opBoolean","SPLIT",FACE,{"disambiguationData":[TD([makeQuery(id+"F23.opExtrude","SWEPT_FACE",FACE,{"disambiguationData":[OSD([subQ3])]})])],"derivedFrom":subQ4}),"instanceName":"1"}),makeQuery(id+"F33.opPattern","COPY",FACE,{"derivedFrom":makeQuery(id+"F27.boolean.opBoolean","SPLIT",FACE,{"disambiguationData":[TD([makeQuery(id+"F23.opExtrude","SWEPT_FACE",FACE,{"disambiguationData":[OSD([subQ0])]})])],"derivedFrom":subQ4}),"instanceName":"1"}),makeQuery(id+"F35.opExtrude","CAP_FACE",FACE,{"disambiguationData":[OSD([sQuery(id+"F34.wireOp",EDGE,"E85"),sQuery(id+"F34.wireOp",EDGE,"E86")])],"isStart":true})]});}
            var sketch = newSketch(context, id + "F36", { "sketchPlane" : qUnion([Q0])});
            skCircle(sketch, "E87", {"center": v(49.37, 0) * mm, "radius": 11 * mm});
            skCircle(sketch, "E88", {"center": v(49.37, 0) * mm, "radius": 19.47 * mm});
            skSolve(sketch);
        }
        {
            var Q0;
            Q0 = qSketchRegion(id + "F36", true);
            extrude(context, id + "F37", {"entities" : qUnion([Q0]), "operationType" : NewBodyOperationType.REMOVE, "oppositeDirection" : true, "depth" : 25 * mm, "offsetDistance" : 25 * mm});
        }
    });
